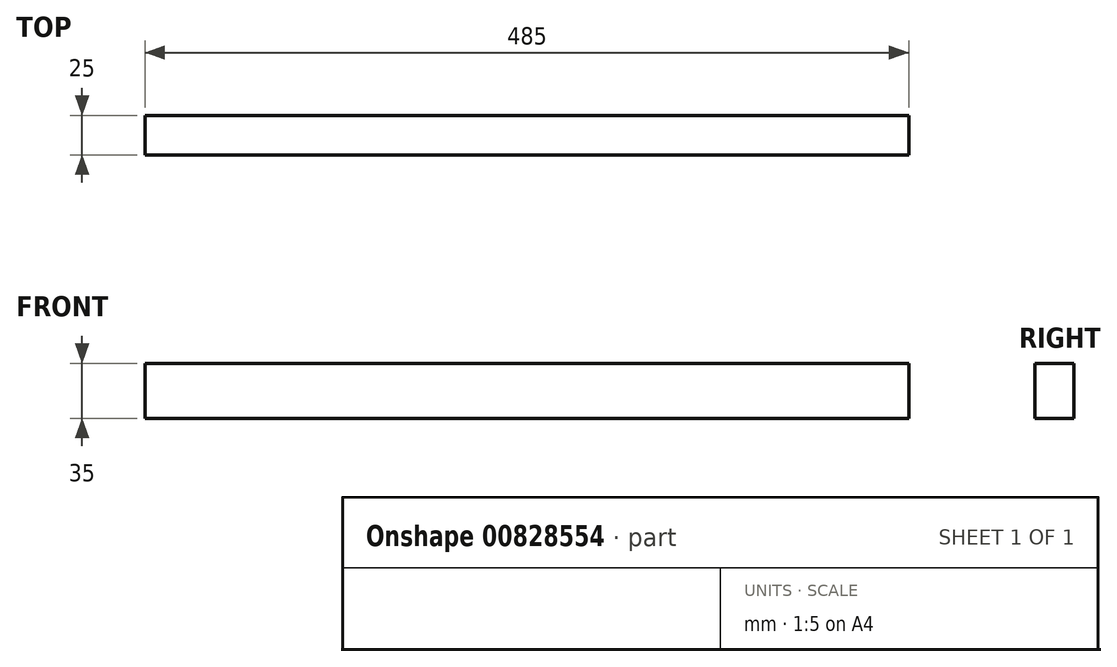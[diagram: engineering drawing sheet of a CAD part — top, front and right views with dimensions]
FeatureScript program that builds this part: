
annotation { "Feature Type Name" : "Feature", "Feature Type Description" : "" }
export const myFeature = defineFeature(function(context is Context, id is Id, definition is map)
    precondition{}
    {
        {
            var Q0;
            Q0=qCreatedBy(makeId("Front.planeOp"),FACE);
            var sketch = newSketch(context, id + "F0", { "sketchPlane" : qUnion([Q0])});
            skLineSegment(sketch, "E0.bottom", {"start": v(-242.5, 35) * mm, "end": v(242.5, 35) * mm});
            skLineSegment(sketch, "E0.top", {"start": v(-242.5, 0) * mm, "end": v(242.5, 0) * mm});
            skLineSegment(sketch, "E0.left", {"start": v(-242.5, 35) * mm, "end": v(-242.5, 0) * mm});
            skLineSegment(sketch, "E0.right", {"start": v(242.5, 35) * mm, "end": v(242.5, 0) * mm});
            skSolve(sketch);
        }
        {
            var Q0;
            Q0=qSketchRegion(id+"F0",true);
            extrude(context, id + "F1", {"entities" : qUnion([Q0]), "depth" : 25 * mm, "offsetDistance" : 25 * mm});
        }
    });
